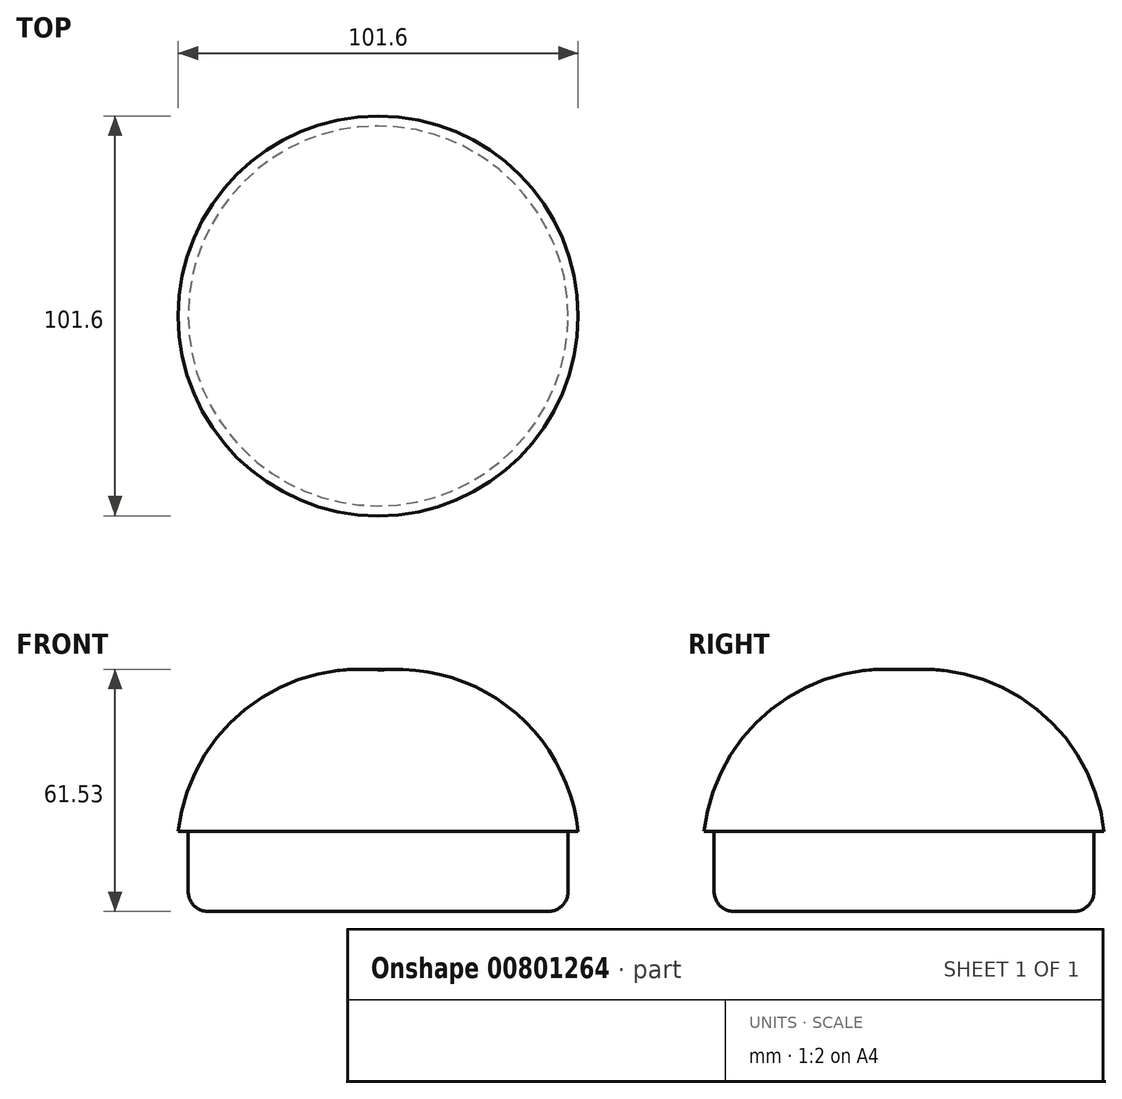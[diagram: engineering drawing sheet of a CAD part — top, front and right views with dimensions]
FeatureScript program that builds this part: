
annotation { "Feature Type Name" : "Feature", "Feature Type Description" : "" }
export const myFeature = defineFeature(function(context is Context, id is Id, definition is map)
    precondition{}
    {
        {
            var Q0;
            Q0=qCreatedBy(makeId("Front.planeOp"),FACE);
            var sketch = newSketch(context, id + "F0", { "sketchPlane" : qUnion([Q0])});
            skLineSegment(sketch, "E0", {"start": v(-28.55, 20.95) * mm, "end": v(22.25, 20.95) * mm});
            skLineSegment(sketch, "E1", {"start": v(-28.55, 20.95) * mm, "end": v(-28.55, -29.85) * mm});
            skArc(sketch, "E2", {"start": v(-28.55, -29.85) * mm, "mid": v(9, -16.6) * mm, "end": v(22.25, 20.95) * mm});
            skSolve(sketch);
        }
        {
            var Q0;
            Q0 = qSketchRegion(id + "F0", true);
            var Q1;
            Q1=sQuery(id+"F0.wireOp",EDGE,"E1");
            revolve(context, id + "F1", {"surfaceOperationType" : NewSurfaceOperationType.NEW, "entities" : qUnion([Q0]), "axis" : qUnion([Q1]), "revolveType" : RevolveType.FULL});
        }
        {
            var Q0;
            Q0=makeQuery(id+"F1.opRevolve","SWEPT_FACE",FACE,{"disambiguationData":[OSD([sQuery(id+"F0.wireOp",EDGE,"E0")])]});
            var sketch = newSketch(context, id + "F2", { "sketchPlane" : qUnion([Q0])});
            skLineSegment(sketch, "E3", {"start": v(22.25, 0) * mm, "end": v(19.7, 0) * mm});
            skCircle(sketch, "E4", {"center": v(-28.55, 0) * mm, "radius": 48.26 * mm});
            skSolve(sketch);
        }
        {
            var Q0;
            Q0 = qSketchRegion(id + "F2", true);
            extrude(context, id + "F3", {"entities" : qUnion([Q0]), "operationType" : NewBodyOperationType.REMOVE, "oppositeDirection" : true, "depth" : 20.32 * mm, "offsetDistance" : 25.4 * mm});
        }
        {
            var Q0;
            Q0=makeQuery(id+"F3.boolean.opBoolean","COPY",EDGE,{"derivedFrom":makeQuery(id+"F3.opExtrude","CAP_EDGE",EDGE,{"disambiguationData":[OSD([sQuery(id+"F2.wireOp",EDGE,"E4")])],"isStart":false})});
            fillet(context, id + "F4", {"entities" : qUnion([Q0]), "radius" : 5.08 * mm, "tangentPropagation" : true, "allowEdgeOverflow" : false});
        }
    });
